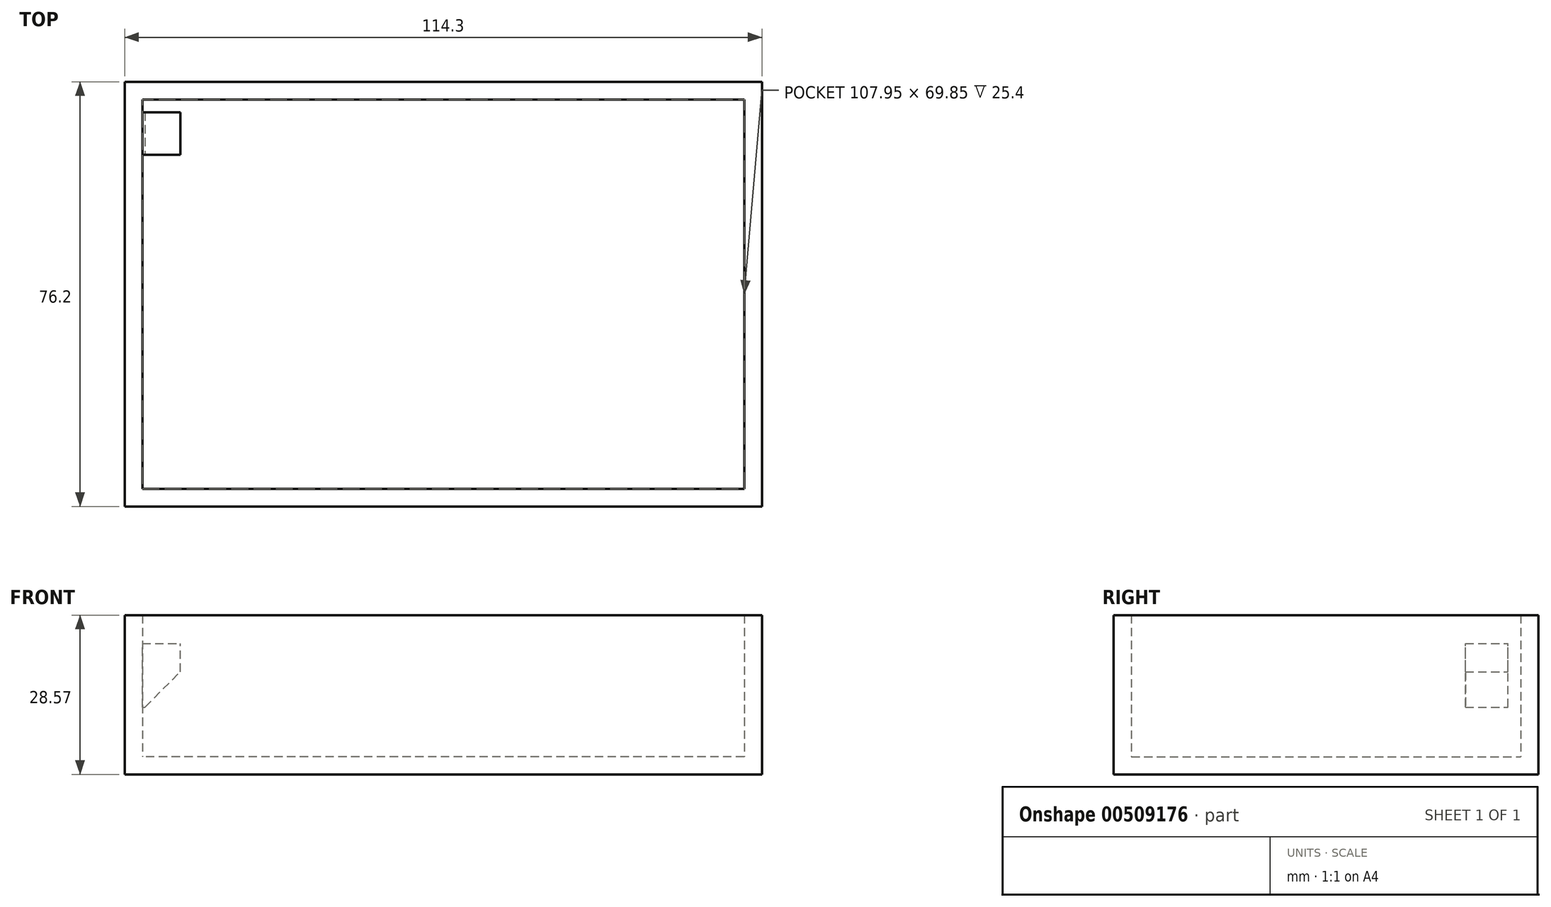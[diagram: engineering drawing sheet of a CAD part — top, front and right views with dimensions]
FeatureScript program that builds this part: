
annotation { "Feature Type Name" : "Feature", "Feature Type Description" : "" }
export const myFeature = defineFeature(function(context is Context, id is Id, definition is map)
    precondition{}
    {
        {
            var Q0;
            Q0=qCreatedBy(makeId("Top.planeOp"),FACE);
            var sketch = newSketch(context, id + "F0", { "sketchPlane" : qUnion([Q0])});
            skLineSegment(sketch, "E0.bottom", {"start": v(57.15, -38.1) * mm, "end": v(-57.15, -38.1) * mm});
            skLineSegment(sketch, "E0.top", {"start": v(57.15, 38.1) * mm, "end": v(-57.15, 38.1) * mm});
            skLineSegment(sketch, "E0.left", {"start": v(57.15, -38.1) * mm, "end": v(57.15, 38.1) * mm});
            skLineSegment(sketch, "E0.right", {"start": v(-57.15, -38.1) * mm, "end": v(-57.15, 38.1) * mm});
            skPoint(sketch, "E0.middle", {"position": v(0, 0) * mm});
            skSolve(sketch);
        }
        {
            var Q0;
            Q0=makeQuery(id+"F0.imprint","IMPRINT",FACE,{"disambiguationData":[TD([[makeQuery(id+"F0.imprint","IMPRINT",EDGE,{"derivedFrom":sQuery(id+"F0.wireOp",EDGE,"E0.bottom")}),-1.0]])]});
            extrude(context, id + "F1", {"entities" : qUnion([Q0]), "depth" : 3.17 * mm});
        }
        {
            var Q0;
            Q0=makeQuery(id+"F1.opExtrude","CAP_FACE",FACE,{"disambiguationData":[OSD([sQuery(id+"F0.wireOp",EDGE,"E0.bottom"),sQuery(id+"F0.wireOp",EDGE,"E0.top"),sQuery(id+"F0.wireOp",EDGE,"E0.left"),sQuery(id+"F0.wireOp",EDGE,"E0.right")])],"isStart":false});
            var sketch = newSketch(context, id + "F2", { "sketchPlane" : qUnion([Q0])});
            skLineSegment(sketch, "E1.bottom", {"start": v(57.15, -38.1) * mm, "end": v(-57.15, -38.1) * mm});
            skLineSegment(sketch, "E1.top", {"start": v(57.15, 38.1) * mm, "end": v(-57.15, 38.1) * mm});
            skLineSegment(sketch, "E1.left", {"start": v(57.15, -38.1) * mm, "end": v(57.15, 38.1) * mm});
            skLineSegment(sketch, "E1.right", {"start": v(-57.15, -38.1) * mm, "end": v(-57.15, 38.1) * mm});
            skPoint(sketch, "E1.middle", {"position": v(0, 0) * mm});
            skLineSegment(sketch, "E2.0", {"start": v(-53.98, -34.92) * mm, "end": v(-53.98, 34.92) * mm});
            skLineSegment(sketch, "E2.1", {"start": v(53.98, -34.92) * mm, "end": v(-53.98, -34.92) * mm});
            skLineSegment(sketch, "E2.2", {"start": v(53.98, -34.92) * mm, "end": v(53.98, 34.92) * mm});
            skLineSegment(sketch, "E2.3", {"start": v(53.98, 34.92) * mm, "end": v(-53.98, 34.92) * mm});
            skSolve(sketch);
        }
        {
            var Q0;
            Q0 = qSketchRegion(id + "F2", true);
            extrude(context, id + "F3", {"entities" : qUnion([Q0]), "operationType" : NewBodyOperationType.ADD, "depth" : 25.4 * mm});
        }
        {
            var Q0;
            Q0=makeQuery(id+"F3.opExtrude","CAP_FACE",FACE,{"disambiguationData":[OSD([sQuery(id+"F2.wireOp",EDGE,"E1.bottom"),sQuery(id+"F2.wireOp",EDGE,"E1.top"),sQuery(id+"F2.wireOp",EDGE,"E1.left"),sQuery(id+"F2.wireOp",EDGE,"E1.right"),sQuery(id+"F2.wireOp",EDGE,"E2.0"),sQuery(id+"F2.wireOp",EDGE,"E2.1"),sQuery(id+"F2.wireOp",EDGE,"E2.2"),sQuery(id+"F2.wireOp",EDGE,"E2.3")])],"isStart":false});
            cPlane(context, id + "F4", {"entities" : qUnion([Q0]), "cplaneType" : CPlaneType.OFFSET, "offset" : 5.08 * mm, "oppositeDirection" : true, "width" : 152.4 * mm, "height" : 152.4 * mm});
        }
        {
            var Q0;
            Q0=qCreatedBy(id+"F4.planeOp",FACE);
            var sketch = newSketch(context, id + "F5", { "sketchPlane" : qUnion([Q0])});
            skLineSegment(sketch, "E3.bottom", {"start": v(-54.78, 32.61) * mm, "end": v(-47.16, 32.61) * mm});
            skLineSegment(sketch, "E3.top", {"start": v(-54.78, 25) * mm, "end": v(-47.16, 25) * mm});
            skLineSegment(sketch, "E3.left", {"start": v(-54.78, 32.61) * mm, "end": v(-54.78, 25) * mm});
            skLineSegment(sketch, "E3.right", {"start": v(-47.16, 32.61) * mm, "end": v(-47.16, 25) * mm});
            skSolve(sketch);
        }
        {
            var Q0;
            Q0 = qSketchRegion(id + "F5", true);
            extrude(context, id + "F6", {"entities" : qUnion([Q0]), "operationType" : NewBodyOperationType.ADD, "oppositeDirection" : true, "depth" : 11.43 * mm});
        }
        {
            var Q0;
            Q0=makeQuery(id+"F6.opExtrude","CAP_EDGE",EDGE,{"disambiguationData":[OSD([sQuery(id+"F5.wireOp",EDGE,"E3.right")])],"isStart":false});
            chamfer(context, id + "F7", {"entities" : qUnion([Q0]), "width" : 6.35 * mm, "tangentPropagation" : true});
        }
    });
